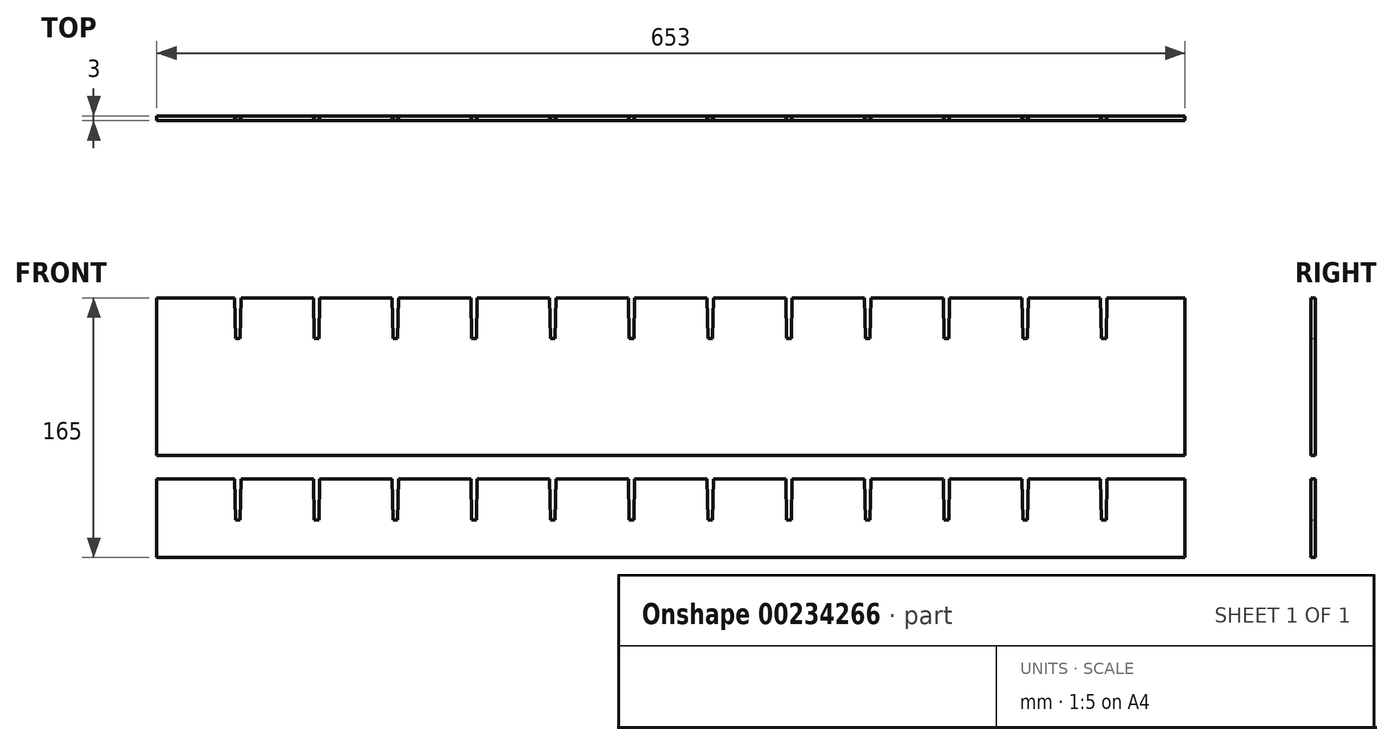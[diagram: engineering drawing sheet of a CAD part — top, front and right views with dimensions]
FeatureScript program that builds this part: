
annotation { "Feature Type Name" : "Feature", "Feature Type Description" : "" }
export const myFeature = defineFeature(function(context is Context, id is Id, definition is map)
    precondition{}
    {
        {
            var Q0;
            Q0=qCreatedBy(makeId("Front.planeOp"),FACE);
            var sketch = newSketch(context, id + "F0", { "sketchPlane" : qUnion([Q0])});
            skLineSegment(sketch, "E0.bottom", {"start": v(0, 0) * mm, "end": v(653, 0) * mm});
            skLineSegment(sketch, "E0.top", {"start": v(0, 100) * mm, "end": v(653, 100) * mm});
            skLineSegment(sketch, "E0.left", {"start": v(0, 0) * mm, "end": v(0, 100) * mm});
            skLineSegment(sketch, "E0.right", {"start": v(653, 0) * mm, "end": v(653, 100) * mm});
            skLineSegment(sketch, "E1", {"start": v(0, 74) * mm, "end": v(653, 74) * mm, "construction": true});
            skLineSegment(sketch, "E2", {"start": v(49.5, 100) * mm, "end": v(50, 74) * mm});
            skLineSegment(sketch, "E3", {"start": v(53, 74) * mm, "end": v(53.5, 100) * mm});
            skLineSegment(sketch, "E4", {"start": v(49.5, 100) * mm, "end": v(53.5, 100) * mm});
            skLineSegment(sketch, "E5", {"start": v(50, 74) * mm, "end": v(53, 74) * mm});
            skPoint(sketch, "E6", {"position": v(51.5, 100) * mm});
            skPoint(sketch, "E7", {"position": v(51.5, 74) * mm});
            skPoint(sketch, "E8.1.0.0", {"position": v(101.5, 100) * mm});
            skLineSegment(sketch, "E8.1.0.1", {"start": v(99.5, 100) * mm, "end": v(100, 74) * mm});
            skLineSegment(sketch, "E8.1.0.2", {"start": v(103, 74) * mm, "end": v(103.5, 100) * mm});
            skPoint(sketch, "E8.1.0.3", {"position": v(101.5, 74) * mm});
            skLineSegment(sketch, "E8.1.0.4", {"start": v(99.5, 100) * mm, "end": v(103.5, 100) * mm});
            skLineSegment(sketch, "E8.1.0.5", {"start": v(100, 74) * mm, "end": v(103, 74) * mm});
            skPoint(sketch, "E8.2.0.0", {"position": v(151.5, 100) * mm});
            skLineSegment(sketch, "E8.2.0.1", {"start": v(149.5, 100) * mm, "end": v(150, 74) * mm});
            skLineSegment(sketch, "E8.2.0.2", {"start": v(153, 74) * mm, "end": v(153.5, 100) * mm});
            skPoint(sketch, "E8.2.0.3", {"position": v(151.5, 74) * mm});
            skLineSegment(sketch, "E8.2.0.4", {"start": v(149.5, 100) * mm, "end": v(153.5, 100) * mm});
            skLineSegment(sketch, "E8.2.0.5", {"start": v(150, 74) * mm, "end": v(153, 74) * mm});
            skPoint(sketch, "E8.3.0.0", {"position": v(201.5, 100) * mm});
            skLineSegment(sketch, "E8.3.0.1", {"start": v(199.5, 100) * mm, "end": v(200, 74) * mm});
            skLineSegment(sketch, "E8.3.0.2", {"start": v(203, 74) * mm, "end": v(203.5, 100) * mm});
            skPoint(sketch, "E8.3.0.3", {"position": v(201.5, 74) * mm});
            skLineSegment(sketch, "E8.3.0.4", {"start": v(199.5, 100) * mm, "end": v(203.5, 100) * mm});
            skLineSegment(sketch, "E8.3.0.5", {"start": v(200, 74) * mm, "end": v(203, 74) * mm});
            skPoint(sketch, "E8.4.0.0", {"position": v(251.5, 100) * mm});
            skLineSegment(sketch, "E8.4.0.1", {"start": v(249.5, 100) * mm, "end": v(250, 74) * mm});
            skLineSegment(sketch, "E8.4.0.2", {"start": v(253, 74) * mm, "end": v(253.5, 100) * mm});
            skPoint(sketch, "E8.4.0.3", {"position": v(251.5, 74) * mm});
            skLineSegment(sketch, "E8.4.0.4", {"start": v(249.5, 100) * mm, "end": v(253.5, 100) * mm});
            skLineSegment(sketch, "E8.4.0.5", {"start": v(250, 74) * mm, "end": v(253, 74) * mm});
            skPoint(sketch, "E8.5.0.0", {"position": v(301.5, 100) * mm});
            skLineSegment(sketch, "E8.5.0.1", {"start": v(299.5, 100) * mm, "end": v(300, 74) * mm});
            skLineSegment(sketch, "E8.5.0.2", {"start": v(303, 74) * mm, "end": v(303.5, 100) * mm});
            skPoint(sketch, "E8.5.0.3", {"position": v(301.5, 74) * mm});
            skLineSegment(sketch, "E8.5.0.4", {"start": v(299.5, 100) * mm, "end": v(303.5, 100) * mm});
            skLineSegment(sketch, "E8.5.0.5", {"start": v(300, 74) * mm, "end": v(303, 74) * mm});
            skPoint(sketch, "E8.6.0.0", {"position": v(351.5, 100) * mm});
            skLineSegment(sketch, "E8.6.0.1", {"start": v(349.5, 100) * mm, "end": v(350, 74) * mm});
            skLineSegment(sketch, "E8.6.0.2", {"start": v(353, 74) * mm, "end": v(353.5, 100) * mm});
            skPoint(sketch, "E8.6.0.3", {"position": v(351.5, 74) * mm});
            skLineSegment(sketch, "E8.6.0.4", {"start": v(349.5, 100) * mm, "end": v(353.5, 100) * mm});
            skLineSegment(sketch, "E8.6.0.5", {"start": v(350, 74) * mm, "end": v(353, 74) * mm});
            skPoint(sketch, "E8.7.0.0", {"position": v(401.5, 100) * mm});
            skLineSegment(sketch, "E8.7.0.1", {"start": v(399.5, 100) * mm, "end": v(400, 74) * mm});
            skLineSegment(sketch, "E8.7.0.2", {"start": v(403, 74) * mm, "end": v(403.5, 100) * mm});
            skPoint(sketch, "E8.7.0.3", {"position": v(401.5, 74) * mm});
            skLineSegment(sketch, "E8.7.0.4", {"start": v(399.5, 100) * mm, "end": v(403.5, 100) * mm});
            skLineSegment(sketch, "E8.7.0.5", {"start": v(400, 74) * mm, "end": v(403, 74) * mm});
            skPoint(sketch, "E8.8.0.0", {"position": v(451.5, 100) * mm});
            skLineSegment(sketch, "E8.8.0.1", {"start": v(449.5, 100) * mm, "end": v(450, 74) * mm});
            skLineSegment(sketch, "E8.8.0.2", {"start": v(453, 74) * mm, "end": v(453.5, 100) * mm});
            skPoint(sketch, "E8.8.0.3", {"position": v(451.5, 74) * mm});
            skLineSegment(sketch, "E8.8.0.4", {"start": v(449.5, 100) * mm, "end": v(453.5, 100) * mm});
            skLineSegment(sketch, "E8.8.0.5", {"start": v(450, 74) * mm, "end": v(453, 74) * mm});
            skPoint(sketch, "E8.9.0.0", {"position": v(501.5, 100) * mm});
            skLineSegment(sketch, "E8.9.0.1", {"start": v(499.5, 100) * mm, "end": v(500, 74) * mm});
            skLineSegment(sketch, "E8.9.0.2", {"start": v(503, 74) * mm, "end": v(503.5, 100) * mm});
            skPoint(sketch, "E8.9.0.3", {"position": v(501.5, 74) * mm});
            skLineSegment(sketch, "E8.9.0.4", {"start": v(499.5, 100) * mm, "end": v(503.5, 100) * mm});
            skLineSegment(sketch, "E8.9.0.5", {"start": v(500, 74) * mm, "end": v(503, 74) * mm});
            skPoint(sketch, "E8.10.0.0", {"position": v(551.5, 100) * mm});
            skLineSegment(sketch, "E8.10.0.1", {"start": v(549.5, 100) * mm, "end": v(550, 74) * mm});
            skLineSegment(sketch, "E8.10.0.2", {"start": v(553, 74) * mm, "end": v(553.5, 100) * mm});
            skPoint(sketch, "E8.10.0.3", {"position": v(551.5, 74) * mm});
            skLineSegment(sketch, "E8.10.0.4", {"start": v(549.5, 100) * mm, "end": v(553.5, 100) * mm});
            skLineSegment(sketch, "E8.10.0.5", {"start": v(550, 74) * mm, "end": v(553, 74) * mm});
            skPoint(sketch, "E8.11.0.0", {"position": v(601.5, 100) * mm});
            skLineSegment(sketch, "E8.11.0.1", {"start": v(599.5, 100) * mm, "end": v(600, 74) * mm});
            skLineSegment(sketch, "E8.11.0.2", {"start": v(603, 74) * mm, "end": v(603.5, 100) * mm});
            skPoint(sketch, "E8.11.0.3", {"position": v(601.5, 74) * mm});
            skLineSegment(sketch, "E8.11.0.4", {"start": v(599.5, 100) * mm, "end": v(603.5, 100) * mm});
            skLineSegment(sketch, "E8.11.0.5", {"start": v(600, 74) * mm, "end": v(603, 74) * mm});
            skLineSegment(sketch, "E8.direction1", {"start": v(50, 74) * mm, "end": v(100, 74) * mm, "construction": true});
            skSolve(sketch);
        }
        {
            var Q0;
            Q0=makeQuery(id+"F0.imprint","IMPRINT",FACE,{"disambiguationData":[TD([[makeQuery(id+"F0.imprint","IMPRINT",EDGE,{"derivedFrom":sQuery(id+"F0.wireOp",EDGE,"E0.bottom")}),1.0]])]});
            extrude(context, id + "F1", {"entities" : qUnion([Q0]), "depth" : 3 * mm});
        }
        {
            var Q0;
            Q0=qCreatedBy(makeId("Front.planeOp"),FACE);
            var sketch = newSketch(context, id + "F2", { "sketchPlane" : qUnion([Q0])});
            skLineSegment(sketch, "E9.bottom", {"start": v(0, -65) * mm, "end": v(653, -65) * mm});
            skLineSegment(sketch, "E9.top", {"start": v(0, -15) * mm, "end": v(653, -15) * mm});
            skLineSegment(sketch, "E9.left", {"start": v(0, -65) * mm, "end": v(0, -15) * mm});
            skLineSegment(sketch, "E9.right", {"start": v(653, -65) * mm, "end": v(653, -15) * mm});
            skLineSegment(sketch, "E10", {"start": v(0, -41) * mm, "end": v(653, -41) * mm, "construction": true});
            skLineSegment(sketch, "E11", {"start": v(49.5, -15) * mm, "end": v(50, -41) * mm});
            skLineSegment(sketch, "E12", {"start": v(53, -41) * mm, "end": v(53.5, -15) * mm});
            skLineSegment(sketch, "E13", {"start": v(49.5, -15) * mm, "end": v(53.5, -15) * mm});
            skLineSegment(sketch, "E14", {"start": v(50, -41) * mm, "end": v(53, -41) * mm});
            skPoint(sketch, "E15", {"position": v(51.5, -15) * mm});
            skPoint(sketch, "E16", {"position": v(51.5, -41) * mm});
            skPoint(sketch, "E17.1.0.0", {"position": v(101.5, -15) * mm});
            skLineSegment(sketch, "E17.1.0.1", {"start": v(99.5, -15) * mm, "end": v(100, -41) * mm});
            skLineSegment(sketch, "E17.1.0.2", {"start": v(103, -41) * mm, "end": v(103.5, -15) * mm});
            skPoint(sketch, "E17.1.0.3", {"position": v(101.5, -41) * mm});
            skLineSegment(sketch, "E17.1.0.4", {"start": v(99.5, -15) * mm, "end": v(103.5, -15) * mm});
            skLineSegment(sketch, "E17.1.0.5", {"start": v(100, -41) * mm, "end": v(103, -41) * mm});
            skPoint(sketch, "E17.2.0.0", {"position": v(151.5, -15) * mm});
            skLineSegment(sketch, "E17.2.0.1", {"start": v(149.5, -15) * mm, "end": v(150, -41) * mm});
            skLineSegment(sketch, "E17.2.0.2", {"start": v(153, -41) * mm, "end": v(153.5, -15) * mm});
            skPoint(sketch, "E17.2.0.3", {"position": v(151.5, -41) * mm});
            skLineSegment(sketch, "E17.2.0.4", {"start": v(149.5, -15) * mm, "end": v(153.5, -15) * mm});
            skLineSegment(sketch, "E17.2.0.5", {"start": v(150, -41) * mm, "end": v(153, -41) * mm});
            skPoint(sketch, "E17.3.0.0", {"position": v(201.5, -15) * mm});
            skLineSegment(sketch, "E17.3.0.1", {"start": v(199.5, -15) * mm, "end": v(200, -41) * mm});
            skLineSegment(sketch, "E17.3.0.2", {"start": v(203, -41) * mm, "end": v(203.5, -15) * mm});
            skPoint(sketch, "E17.3.0.3", {"position": v(201.5, -41) * mm});
            skLineSegment(sketch, "E17.3.0.4", {"start": v(199.5, -15) * mm, "end": v(203.5, -15) * mm});
            skLineSegment(sketch, "E17.3.0.5", {"start": v(200, -41) * mm, "end": v(203, -41) * mm});
            skPoint(sketch, "E17.4.0.0", {"position": v(251.5, -15) * mm});
            skLineSegment(sketch, "E17.4.0.1", {"start": v(249.5, -15) * mm, "end": v(250, -41) * mm});
            skLineSegment(sketch, "E17.4.0.2", {"start": v(253, -41) * mm, "end": v(253.5, -15) * mm});
            skPoint(sketch, "E17.4.0.3", {"position": v(251.5, -41) * mm});
            skLineSegment(sketch, "E17.4.0.4", {"start": v(249.5, -15) * mm, "end": v(253.5, -15) * mm});
            skLineSegment(sketch, "E17.4.0.5", {"start": v(250, -41) * mm, "end": v(253, -41) * mm});
            skPoint(sketch, "E17.5.0.0", {"position": v(301.5, -15) * mm});
            skLineSegment(sketch, "E17.5.0.1", {"start": v(299.5, -15) * mm, "end": v(300, -41) * mm});
            skLineSegment(sketch, "E17.5.0.2", {"start": v(303, -41) * mm, "end": v(303.5, -15) * mm});
            skPoint(sketch, "E17.5.0.3", {"position": v(301.5, -41) * mm});
            skLineSegment(sketch, "E17.5.0.4", {"start": v(299.5, -15) * mm, "end": v(303.5, -15) * mm});
            skLineSegment(sketch, "E17.5.0.5", {"start": v(300, -41) * mm, "end": v(303, -41) * mm});
            skPoint(sketch, "E17.6.0.0", {"position": v(351.5, -15) * mm});
            skLineSegment(sketch, "E17.6.0.1", {"start": v(349.5, -15) * mm, "end": v(350, -41) * mm});
            skLineSegment(sketch, "E17.6.0.2", {"start": v(353, -41) * mm, "end": v(353.5, -15) * mm});
            skPoint(sketch, "E17.6.0.3", {"position": v(351.5, -41) * mm});
            skLineSegment(sketch, "E17.6.0.4", {"start": v(349.5, -15) * mm, "end": v(353.5, -15) * mm});
            skLineSegment(sketch, "E17.6.0.5", {"start": v(350, -41) * mm, "end": v(353, -41) * mm});
            skPoint(sketch, "E17.7.0.0", {"position": v(401.5, -15) * mm});
            skLineSegment(sketch, "E17.7.0.1", {"start": v(399.5, -15) * mm, "end": v(400, -41) * mm});
            skLineSegment(sketch, "E17.7.0.2", {"start": v(403, -41) * mm, "end": v(403.5, -15) * mm});
            skPoint(sketch, "E17.7.0.3", {"position": v(401.5, -41) * mm});
            skLineSegment(sketch, "E17.7.0.4", {"start": v(399.5, -15) * mm, "end": v(403.5, -15) * mm});
            skLineSegment(sketch, "E17.7.0.5", {"start": v(400, -41) * mm, "end": v(403, -41) * mm});
            skPoint(sketch, "E17.8.0.0", {"position": v(451.5, -15) * mm});
            skLineSegment(sketch, "E17.8.0.1", {"start": v(449.5, -15) * mm, "end": v(450, -41) * mm});
            skLineSegment(sketch, "E17.8.0.2", {"start": v(453, -41) * mm, "end": v(453.5, -15) * mm});
            skPoint(sketch, "E17.8.0.3", {"position": v(451.5, -41) * mm});
            skLineSegment(sketch, "E17.8.0.4", {"start": v(449.5, -15) * mm, "end": v(453.5, -15) * mm});
            skLineSegment(sketch, "E17.8.0.5", {"start": v(450, -41) * mm, "end": v(453, -41) * mm});
            skPoint(sketch, "E17.9.0.0", {"position": v(501.5, -15) * mm});
            skLineSegment(sketch, "E17.9.0.1", {"start": v(499.5, -15) * mm, "end": v(500, -41) * mm});
            skLineSegment(sketch, "E17.9.0.2", {"start": v(503, -41) * mm, "end": v(503.5, -15) * mm});
            skPoint(sketch, "E17.9.0.3", {"position": v(501.5, -41) * mm});
            skLineSegment(sketch, "E17.9.0.4", {"start": v(499.5, -15) * mm, "end": v(503.5, -15) * mm});
            skLineSegment(sketch, "E17.9.0.5", {"start": v(500, -41) * mm, "end": v(503, -41) * mm});
            skPoint(sketch, "E17.10.0.0", {"position": v(551.5, -15) * mm});
            skLineSegment(sketch, "E17.10.0.1", {"start": v(549.5, -15) * mm, "end": v(550, -41) * mm});
            skLineSegment(sketch, "E17.10.0.2", {"start": v(553, -41) * mm, "end": v(553.5, -15) * mm});
            skPoint(sketch, "E17.10.0.3", {"position": v(551.5, -41) * mm});
            skLineSegment(sketch, "E17.10.0.4", {"start": v(549.5, -15) * mm, "end": v(553.5, -15) * mm});
            skLineSegment(sketch, "E17.10.0.5", {"start": v(550, -41) * mm, "end": v(553, -41) * mm});
            skPoint(sketch, "E17.11.0.0", {"position": v(601.5, -15) * mm});
            skLineSegment(sketch, "E17.11.0.1", {"start": v(599.5, -15) * mm, "end": v(600, -41) * mm});
            skLineSegment(sketch, "E17.11.0.2", {"start": v(603, -41) * mm, "end": v(603.5, -15) * mm});
            skPoint(sketch, "E17.11.0.3", {"position": v(601.5, -41) * mm});
            skLineSegment(sketch, "E17.11.0.4", {"start": v(599.5, -15) * mm, "end": v(603.5, -15) * mm});
            skLineSegment(sketch, "E17.11.0.5", {"start": v(600, -41) * mm, "end": v(603, -41) * mm});
            skLineSegment(sketch, "E17.direction1", {"start": v(50, -41) * mm, "end": v(100, -41) * mm, "construction": true});
            skSolve(sketch);
        }
        {
            var Q0;
            Q0=makeQuery(id+"F2.imprint","IMPRINT",FACE,{"disambiguationData":[TD([[makeQuery(id+"F2.imprint","IMPRINT",EDGE,{"derivedFrom":sQuery(id+"F2.wireOp",EDGE,"E9.bottom")}),1.0]])]});
            extrude(context, id + "F3", {"entities" : qUnion([Q0]), "depth" : 3 * mm});
        }
    });
